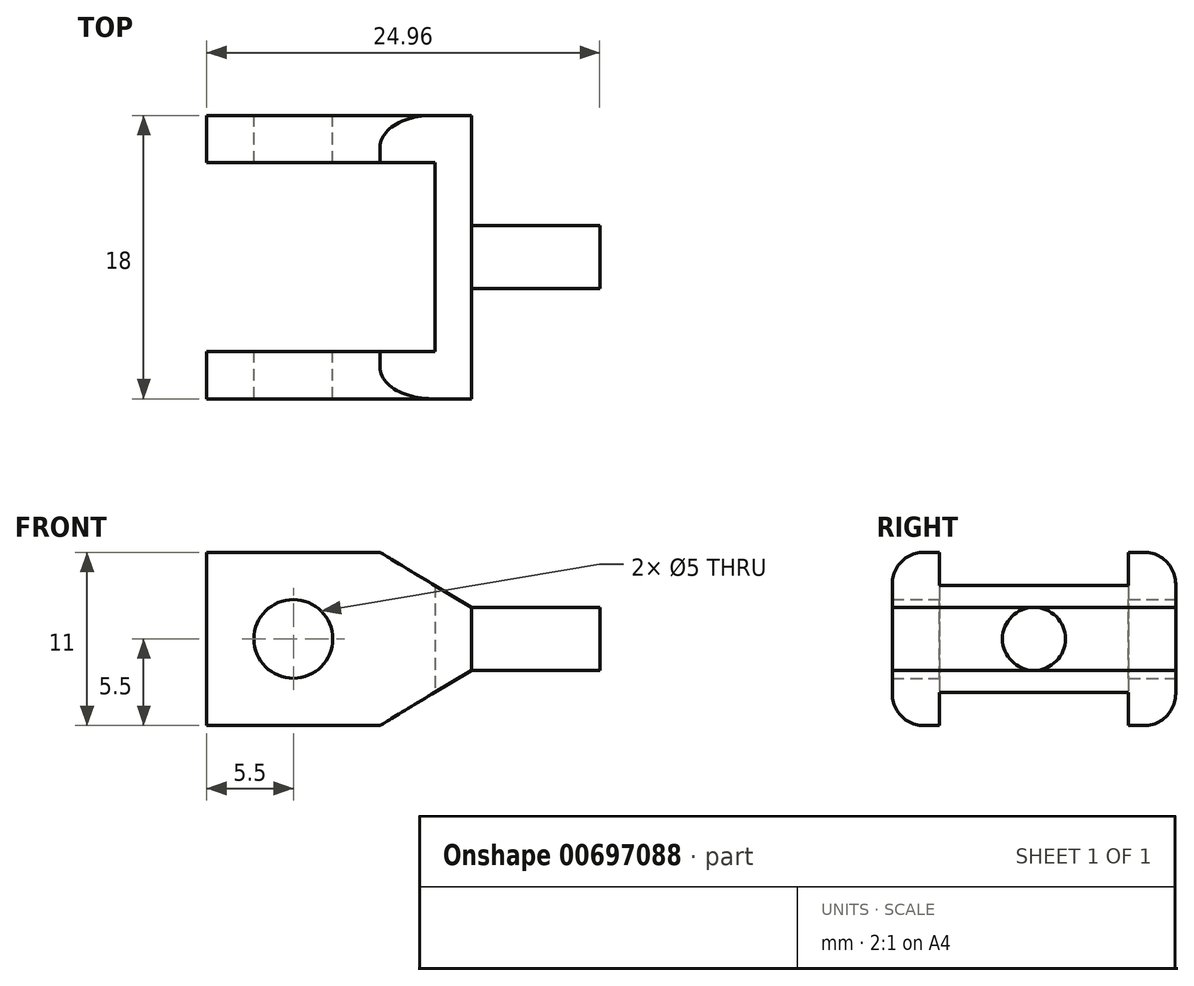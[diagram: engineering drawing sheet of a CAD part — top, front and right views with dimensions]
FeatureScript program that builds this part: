
annotation { "Feature Type Name" : "Feature", "Feature Type Description" : "" }
export const myFeature = defineFeature(function(context is Context, id is Id, definition is map)
    precondition{}
    {
        {
            assignVariable(context, id + "F0", {"name" : "wall_thickness", "anyValue" : 3});
        }
        {
            assignVariable(context, id + "F1", {"name" : "attachment_thickness", "anyValue" : 10});
        }
        {
            assignVariable(context, id + "F2", {"name" : "attachment_adj", "anyValue" : 2});
        }
        {
            var Q0;
            Q0=qCreatedBy(makeId("Front.planeOp"),FACE);
            var sketch = newSketch(context, id + "F3", { "sketchPlane" : qUnion([Q0])});
            skCircle(sketch, "E0", {"center": v(-9, -1.5) * mm, "radius": 2.5 * mm});
            skLineSegment(sketch, "E1", {"start": v(-3.5, -1.5) * mm, "end": v(-6.5, -1.5) * mm});
            skLineSegment(sketch, "E2", {"start": v(-9, 1) * mm, "end": v(-9, 4) * mm});
            skLineSegment(sketch, "E3", {"start": v(-9, 4) * mm, "end": v(-3.5, 4) * mm});
            skLineSegment(sketch, "E4", {"start": v(-9, -4) * mm, "end": v(-9, -7) * mm});
            skLineSegment(sketch, "E5", {"start": v(-9, -7) * mm, "end": v(-3.5, -7) * mm});
            skLineSegment(sketch, "E6", {"start": v(-9, 4) * mm, "end": v(-14.5, 4) * mm});
            skLineSegment(sketch, "E7", {"start": v(-14.5, 4) * mm, "end": v(-14.5, -1.5) * mm});
            skLineSegment(sketch, "E8", {"start": v(-14.5, -1.5) * mm, "end": v(-11.5, -1.5) * mm});
            skLineSegment(sketch, "E9", {"start": v(-14.5, -1.5) * mm, "end": v(-14.5, -7) * mm});
            skLineSegment(sketch, "E10", {"start": v(-14.5, -7) * mm, "end": v(-9, -7) * mm});
            skLineSegment(sketch, "E11", {"start": v(2.3, -1.5) * mm, "end": v(2.3, 0.5) * mm});
            skLineSegment(sketch, "E12", {"start": v(2.3, -1.5) * mm, "end": v(2.3, -3.5) * mm});
            skLineSegment(sketch, "E13", {"start": v(2.3, -1.5) * mm, "end": v(10.46, -1.5) * mm});
            skLineSegment(sketch, "E14", {"start": v(10.46, -1.5) * mm, "end": v(10.46, -3.5) * mm});
            skLineSegment(sketch, "E15", {"start": v(10.46, -3.5) * mm, "end": v(2.3, -3.5) * mm});
            skLineSegment(sketch, "E16", {"start": v(-3.5, 4) * mm, "end": v(-3.5, -1.5) * mm});
            skLineSegment(sketch, "E17", {"start": v(-3.5, -1.5) * mm, "end": v(-3.5, -7) * mm});
            skLineSegment(sketch, "E18", {"start": v(-3.5, -1.5) * mm, "end": v(2.3, -1.5) * mm});
            skLineSegment(sketch, "E19", {"start": v(2.3, 0.5) * mm, "end": v(10.46, 0.5) * mm});
            skLineSegment(sketch, "E20", {"start": v(10.46, 0.5) * mm, "end": v(10.46, -1.5) * mm});
            skLineSegment(sketch, "E21", {"start": v(0, 1.9) * mm, "end": v(0, -4.9) * mm});
            skLineSegment(sketch, "E22", {"start": v(0, -1.5) * mm, "end": v(-9, -1.5) * mm});
            skLineSegment(sketch, "E23", {"start": v(-3.5, -7) * mm, "end": v(2.3, -3.5) * mm});
            skLineSegment(sketch, "E24", {"start": v(-3.5, 4) * mm, "end": v(2.3, 0.5) * mm});
            skSolve(sketch);
        }
        {
            var Q0;
            Q0=makeQuery(id+"F3.imprint","IMPRINT",FACE,{"disambiguationData":[TD([[makeQuery(id+"F3.imprint","IMPRINT",EDGE,{"derivedFrom":sQuery(id+"F3.wireOp",EDGE,"E12")}),1.0]])]});
            var Q1;
            Q1=sQuery(id+"F3.wireOp",EDGE,"E13");
            revolve(context, id + "F4", {"surfaceOperationType" : NewSurfaceOperationType.NEW, "entities" : qUnion([Q0]), "axis" : qUnion([Q1]), "revolveType" : RevolveType.FULL});
        }
        {
            var Q0;
            {var subQ0=sQuery(id+"F3.wireOp",EDGE,"E1");Q0=makeQuery(id+"F3.imprint","IMPRINT",FACE,{"disambiguationData":[TD([[makeQuery(id+"F3.imprint","IMPRINT",EDGE,{"derivedFrom":subQ0}),-1.0]])]});}
            var Q1;
            {var subQ0=sQuery(id+"F3.wireOp",EDGE,"E1");Q1=makeQuery(id+"F3.imprint","IMPRINT",FACE,{"disambiguationData":[TD([[makeQuery(id+"F3.imprint","IMPRINT",EDGE,{"derivedFrom":subQ0}),1.0]])]});}
            var Q2;
            {var subQ1=sQuery(id+"F3.wireOp",EDGE,"E4");Q2=makeQuery(id+"F3.imprint","IMPRINT",FACE,{"disambiguationData":[TD([[makeQuery(id+"F3.imprint","IMPRINT",EDGE,{"derivedFrom":subQ1}),-1.0]])]});}
            var Q3;
            {var subQ0=sQuery(id+"F3.wireOp",EDGE,"E2");Q3=makeQuery(id+"F3.imprint","IMPRINT",FACE,{"disambiguationData":[TD([[makeQuery(id+"F3.imprint","IMPRINT",EDGE,{"derivedFrom":subQ0}),1.0]])]});}
            var Q4;
            {var subQ0=sQuery(id+"F3.wireOp",EDGE,"yS7tqIph-VR82-X1AM-3WxU-hnLSQLPVObid");Q4=makeQuery(id+"F3.imprint","IMPRINT",FACE,{"disambiguationData":[TD([[makeQuery(id+"F3.imprint","IMPRINT",EDGE,{"derivedFrom":subQ0}),1.0]])]});}
            var Q5;
            {var subQ4=sQuery(id+"F3.wireOp",EDGE,"gJfknZxP-Udm7-pyeO-u1a5-izMC2o7fMy0n");Q5=makeQuery(id+"F3.imprint","IMPRINT",FACE,{"disambiguationData":[TD([[makeQuery(id+"F3.imprint","IMPRINT",EDGE,{"derivedFrom":subQ4}),1.0]])]});}
            var Q6;
            {var subQ1=sQuery(id+"F3.wireOp",EDGE,"E2");Q6=makeQuery(id+"F3.imprint","IMPRINT",FACE,{"disambiguationData":[TD([[makeQuery(id+"F3.imprint","IMPRINT",EDGE,{"derivedFrom":subQ1}),-1.0]])]});}
            var Q7;
            {var subQ1=sQuery(id+"F3.wireOp",EDGE,"E4");Q7=makeQuery(id+"F3.imprint","IMPRINT",FACE,{"disambiguationData":[TD([[makeQuery(id+"F3.imprint","IMPRINT",EDGE,{"derivedFrom":subQ1}),1.0]])]});}
            var Q8;
            Q8=makeQuery(id+"F3.imprint","IMPRINT",FACE,{"disambiguationData":[TD([[makeQuery(id+"F3.imprint","IMPRINT",EDGE,{"derivedFrom":sQuery(id+"F3.wireOp",EDGE,"E11")}),1.0]])]});
            var Q9;
            Q9=makeQuery(id+"F3.imprint","IMPRINT",FACE,{"disambiguationData":[TD([[makeQuery(id+"F3.imprint","IMPRINT",EDGE,{"derivedFrom":sQuery(id+"F3.wireOp",EDGE,"E12")}),-1.0]])]});
            var Q10;
            {var subQ1=sQuery(id+"F3.wireOp",EDGE,"E16");Q10=makeQuery(id+"F3.imprint","IMPRINT",FACE,{"disambiguationData":[TD([[makeQuery(id+"F3.imprint","IMPRINT",EDGE,{"derivedFrom":subQ1}),1.0]])]});}
            var Q11;
            {var subQ1=sQuery(id+"F3.wireOp",EDGE,"E17");Q11=makeQuery(id+"F3.imprint","IMPRINT",FACE,{"disambiguationData":[TD([[makeQuery(id+"F3.imprint","IMPRINT",EDGE,{"derivedFrom":subQ1}),1.0]])]});}
            extrude(context, id + "F5", {"entities" : qUnion([Q0, Q1, Q2, Q3, Q4, Q5, Q6, Q7, Q8, Q9, Q10, Q11]), "endBound" : BoundingType.SYMMETRIC, "depth" : (2 * getVariable(context, 'wall_thickness') + getVariable(context, 'attachment_thickness') + getVariable(context, 'attachment_adj')) * mm, "offsetDistance" : 25 * mm});
        }
        {
            var Q0;
            {var subQ0=sQuery(id+"F3.wireOp",EDGE,"E2");Q0=makeQuery(id+"F3.imprint","IMPRINT",FACE,{"disambiguationData":[TD([[makeQuery(id+"F3.imprint","IMPRINT",EDGE,{"derivedFrom":subQ0}),1.0]])]});}
            var Q1;
            {var subQ0=sQuery(id+"F3.wireOp",EDGE,"E1");Q1=makeQuery(id+"F3.imprint","IMPRINT",FACE,{"disambiguationData":[TD([[makeQuery(id+"F3.imprint","IMPRINT",EDGE,{"derivedFrom":subQ0}),-1.0]])]});}
            var Q2;
            {var subQ0=sQuery(id+"F3.wireOp",EDGE,"E1");Q2=makeQuery(id+"F3.imprint","IMPRINT",FACE,{"disambiguationData":[TD([[makeQuery(id+"F3.imprint","IMPRINT",EDGE,{"derivedFrom":subQ0}),1.0]])]});}
            var Q3;
            {var subQ1=sQuery(id+"F3.wireOp",EDGE,"E4");Q3=makeQuery(id+"F3.imprint","IMPRINT",FACE,{"disambiguationData":[TD([[makeQuery(id+"F3.imprint","IMPRINT",EDGE,{"derivedFrom":subQ1}),-1.0]])]});}
            var Q4;
            {var subQ1=sQuery(id+"F3.wireOp",EDGE,"E2");Q4=makeQuery(id+"F3.imprint","IMPRINT",FACE,{"disambiguationData":[TD([[makeQuery(id+"F3.imprint","IMPRINT",EDGE,{"derivedFrom":subQ1}),-1.0]])]});}
            var Q5;
            {var subQ1=sQuery(id+"F3.wireOp",EDGE,"E4");Q5=makeQuery(id+"F3.imprint","IMPRINT",FACE,{"disambiguationData":[TD([[makeQuery(id+"F3.imprint","IMPRINT",EDGE,{"derivedFrom":subQ1}),1.0]])]});}
            var Q6;
            {var subQ1=sQuery(id+"F3.wireOp",EDGE,"E16");Q6=makeQuery(id+"F3.imprint","IMPRINT",FACE,{"disambiguationData":[TD([[makeQuery(id+"F3.imprint","IMPRINT",EDGE,{"derivedFrom":subQ1}),1.0]])]});}
            var Q7;
            {var subQ1=sQuery(id+"F3.wireOp",EDGE,"E17");Q7=makeQuery(id+"F3.imprint","IMPRINT",FACE,{"disambiguationData":[TD([[makeQuery(id+"F3.imprint","IMPRINT",EDGE,{"derivedFrom":subQ1}),1.0]])]});}
            extrude(context, id + "F6", {"entities" : qUnion([Q0, Q1, Q2, Q3, Q4, Q5, Q6, Q7]), "endBound" : BoundingType.SYMMETRIC, "depth" : (getVariable(context, 'attachment_thickness') + getVariable(context, 'attachment_adj')) * mm, "offsetDistance" : 25 * mm});
        }
        {
            var Q0;
            Q0=makeQuery(id+"F6.opExtrude","SWEPT_BODY",BODY,{"disambiguationData":[OSD([sQuery(id+"F3.wireOp",EDGE,"SgepJQXq-TUmh-nhVi-3rq4-fWczkHmfWS6F"),sQuery(id+"F3.wireOp",EDGE,"E0"),sQuery(id+"F3.wireOp",EDGE,"E3"),sQuery(id+"F3.wireOp",EDGE,"ngwlcmQv-9yvB-s5Ri-OHHn-qTRzw7BkK21Q"),sQuery(id+"F3.wireOp",EDGE,"E5"),sQuery(id+"F3.wireOp",EDGE,"zXwatqiV-mbqh-733I-NthZ-ha7flQUijGAv"),sQuery(id+"F3.wireOp",EDGE,"E6"),sQuery(id+"F3.wireOp",EDGE,"E7"),sQuery(id+"F3.wireOp",EDGE,"E9"),sQuery(id+"F3.wireOp",EDGE,"E10")])]});
            var Q1;
            Q1=makeQuery(id+"F5.opExtrude","SWEPT_BODY",BODY,{"disambiguationData":[OSD([sQuery(id+"F3.wireOp",EDGE,"LC9UsJ73-DbBn-lgen-rQoP-FZ1G1hUeGd9N"),sQuery(id+"F3.wireOp",EDGE,"yS7tqIph-VR82-X1AM-3WxU-hnLSQLPVObid"),sQuery(id+"F3.wireOp",EDGE,"E0"),sQuery(id+"F3.wireOp",EDGE,"E3"),sQuery(id+"F3.wireOp",EDGE,"ngwlcmQv-9yvB-s5Ri-OHHn-qTRzw7BkK21Q"),sQuery(id+"F3.wireOp",EDGE,"E5"),sQuery(id+"F3.wireOp",EDGE,"zXwatqiV-mbqh-733I-NthZ-ha7flQUijGAv"),sQuery(id+"F3.wireOp",EDGE,"E6"),sQuery(id+"F3.wireOp",EDGE,"E7"),sQuery(id+"F3.wireOp",EDGE,"E9"),sQuery(id+"F3.wireOp",EDGE,"E10"),sQuery(id+"F3.wireOp",EDGE,"E11"),sQuery(id+"F3.wireOp",EDGE,"E12")])]});
            booleanBodies(context, id + "F7", {"operationType" : BooleanOperationType.SUBTRACTION, "tools" : qUnion([Q0]), "targets" : qUnion([Q1])});
        }
        {
            var Q0;
            Q0=makeQuery(id+"F5.opExtrude","CAP_EDGE",EDGE,{"disambiguationData":[OSD([sQuery(id+"F3.wireOp",EDGE,"E3"),sQuery(id+"F3.wireOp",EDGE,"E6")])],"isStart":false});
            var Q1;
            Q1=makeQuery(id+"F5.opExtrude","CAP_EDGE",EDGE,{"disambiguationData":[OSD([sQuery(id+"F3.wireOp",EDGE,"E5"),sQuery(id+"F3.wireOp",EDGE,"E10")])],"isStart":false});
            var Q2;
            Q2=makeQuery(id+"F5.opExtrude","CAP_EDGE",EDGE,{"disambiguationData":[OSD([sQuery(id+"F3.wireOp",EDGE,"E5"),sQuery(id+"F3.wireOp",EDGE,"E10")])],"isStart":true});
            var Q3;
            Q3=makeQuery(id+"F5.opExtrude","CAP_EDGE",EDGE,{"disambiguationData":[OSD([sQuery(id+"F3.wireOp",EDGE,"E3"),sQuery(id+"F3.wireOp",EDGE,"E6")])],"isStart":true});
            fillet(context, id + "F8", {"entities" : qUnion([Q0, Q1, Q2, Q3]), "radius" : 2 * mm, "tangentPropagation" : true, "allowEdgeOverflow" : false});
        }
    });
